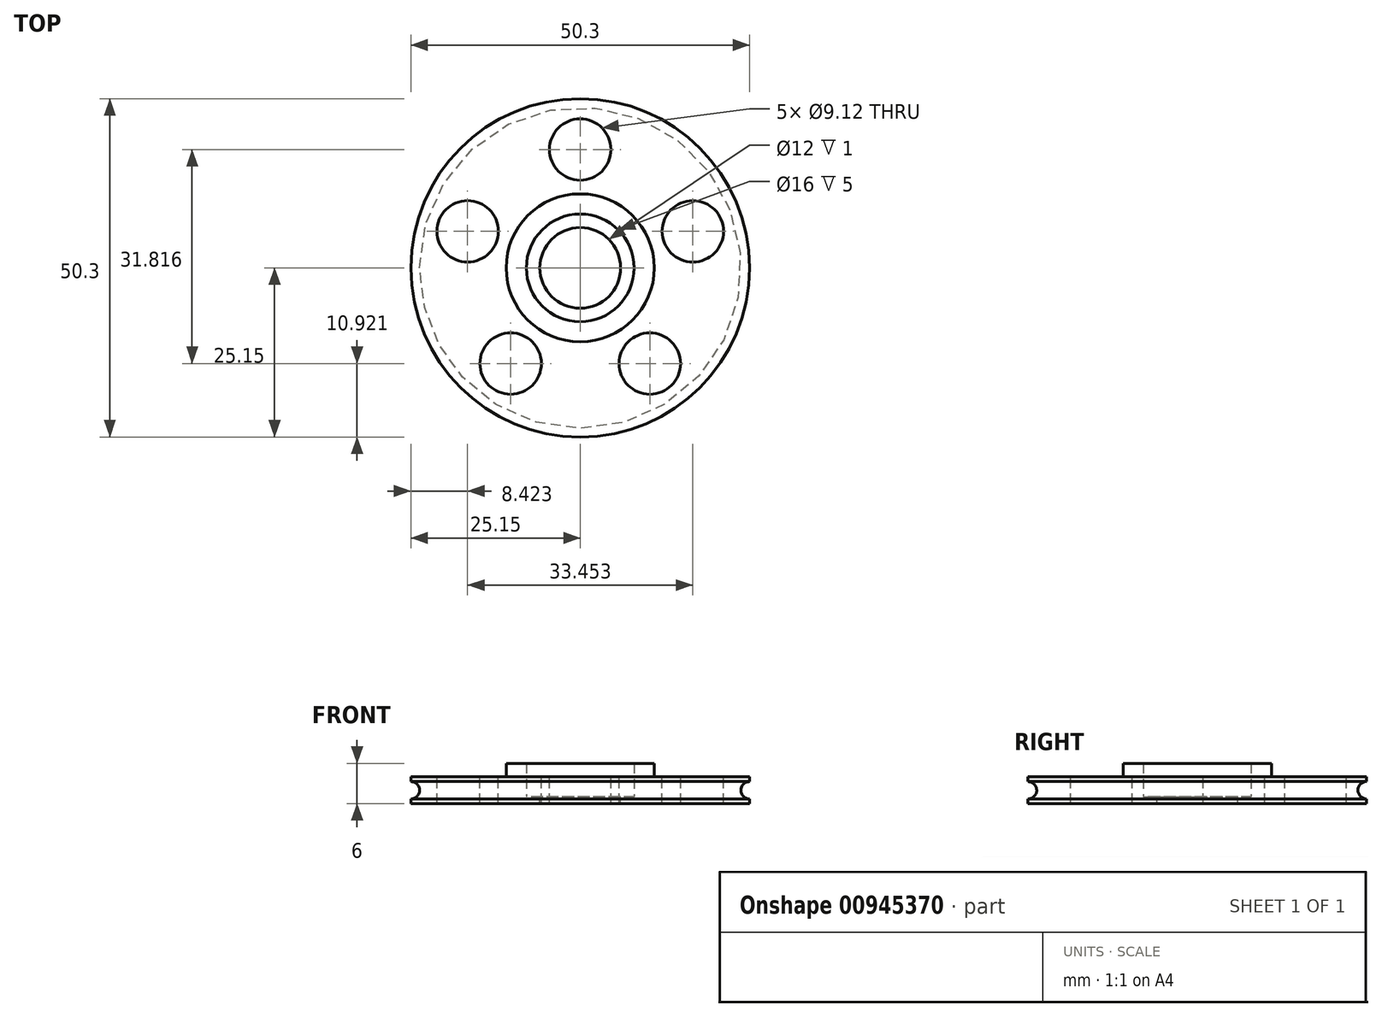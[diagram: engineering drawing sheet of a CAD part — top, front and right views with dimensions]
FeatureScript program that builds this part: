
annotation { "Feature Type Name" : "Feature", "Feature Type Description" : "" }
export const myFeature = defineFeature(function(context is Context, id is Id, definition is map)
    precondition{}
    {
        {
            var Q0;
            Q0=qCreatedBy(makeId("Top.planeOp"),FACE);
            var sketch = newSketch(context, id + "F0", { "sketchPlane" : qUnion([Q0])});
            skCircle(sketch, "E0", {"center": v(0, 0) * mm, "radius": 25.15 * mm});
            skSolve(sketch);
        }
        {
            var Q0;
            Q0=makeQuery(id+"F0.imprint","IMPRINT",FACE,{"disambiguationData":[TD([[makeQuery(id+"F0.imprint","IMPRINT",EDGE,{"derivedFrom":sQuery(id+"F0.wireOp",EDGE,"E0")}),1.0]])]});
            extrude(context, id + "F1", {"entities" : qUnion([Q0]), "depth" : 4 * mm, "offsetDistance" : 25.4 * mm});
        }
        {
            var Q0;
            Q0=makeQuery(id+"F1.opExtrude","CAP_FACE",FACE,{"disambiguationData":[OSD([sQuery(id+"F0.wireOp",EDGE,"E0"),sQuery(id+"F0.wireOp",EDGE,"n39IqKt5-bk1q-LU1x-fgod-8OyBNiFTd7FZ")])],"isStart":false});
            var sketch = newSketch(context, id + "F2", { "sketchPlane" : qUnion([Q0])});
            skCircle(sketch, "E1", {"center": v(0, 0) * mm, "radius": 8 * mm});
            skCircle(sketch, "E2.0", {"center": v(0, 0) * mm, "radius": 11 * mm});
            skSolve(sketch);
        }
        {
            var Q0;
            Q0=qSketchRegion(id+"F2",true);
            extrude(context, id + "F3", {"entities" : qUnion([Q0]), "operationType" : NewBodyOperationType.ADD, "flatOperationType" : FlatOperationType.REMOVE, "depth" : 2 * mm, "offsetDistance" : 25.4 * mm, "domain" : OperationDomain.MODEL});
        }
        {
            var Q0;
            Q0=makeQuery(id+"F3.boolean.opBoolean","SPLIT",FACE,{"disambiguationData":[TD([makeQuery(id+"F3.opExtrude","SWEPT_FACE",FACE,{"disambiguationData":[OSD([sQuery(id+"F2.wireOp",EDGE,"E1")])]})])],"derivedFrom":makeQuery(id+"F1.opExtrude","CAP_FACE",FACE,{"disambiguationData":[OSD([sQuery(id+"F0.wireOp",EDGE,"E0")])],"isStart":false})});
            var sketch = newSketch(context, id + "F4", { "sketchPlane" : qUnion([Q0])});
            skCircle(sketch, "E3", {"center": v(0, 0) * mm, "radius": 6 * mm});
            skSolve(sketch);
        }
        {
            var Q0;
            Q0=makeQuery(id+"F4.imprint","IMPRINT",FACE,{"disambiguationData":[TD([[makeQuery(id+"F4.imprint","IMPRINT",EDGE,{"derivedFrom":sQuery(id+"F4.wireOp",EDGE,"E3")}),1.0]])]});
            var Q1;
            Q1=makeQuery(id+"F4.imprint","IMPRINT",FACE,{"disambiguationData":[TD([[makeQuery(id+"F4.imprint","IMPRINT",EDGE,{"derivedFrom":makeQuery(id+"FgYK8jIepfClWtA_1.opExtrude","CAP_EDGE",EDGE,{"disambiguationData":[OSD([sQuery(id+"F8DXjnVyigKkjng_1.wireOp",EDGE,"EUjAMsCd-Zx2B-3j4q-cP5o-T3GrjTijNDqK")])],"isStart":false})}),1.0]])]});
            extrude(context, id + "F5", {"entities" : qUnion([Q0, Q1]), "operationType" : NewBodyOperationType.REMOVE, "oppositeDirection" : true, "depth" : 9 * mm, "offsetDistance" : 25.4 * mm});
        }
        {
            var Q0;
            Q0=qCreatedBy(makeId("Front.planeOp"),FACE);
            var sketch = newSketch(context, id + "F6", { "sketchPlane" : qUnion([Q0])});
            skCircle(sketch, "E4", {"center": v(-27.3, 2) * mm, "radius": 1.5 * mm});
            skLineSegment(sketch, "E5.bottom", {"start": v(-25.8, 0.65) * mm, "end": v(-27.95, 0.65) * mm});
            skLineSegment(sketch, "E5.top", {"start": v(-25.8, 3.35) * mm, "end": v(-27.95, 3.35) * mm});
            skLineSegment(sketch, "E5.left", {"start": v(-25.8, 0.65) * mm, "end": v(-25.8, 3.35) * mm});
            skLineSegment(sketch, "E5.right", {"start": v(-28.8, 1.91) * mm, "end": v(-28.8, 2.09) * mm});
            skLineSegment(sketch, "E6", {"start": v(0, 19.1) * mm, "end": v(0, -12.61) * mm, "construction": true});
            skLineSegment(sketch, "E7", {"start": v(-25.8, 1.83) * mm, "end": v(-25.81, 1.83) * mm});
            skPoint(sketch, "E8.orphan", {"position": v(-38.97, 3.35) * mm});
            skPoint(sketch, "E9.end.orphan", {"position": v(-15.64, 0.65) * mm});
            skPoint(sketch, "E9.start.orphan", {"position": v(-25.8, 2) * mm});
            skSolve(sketch);
        }
        {
            var Q0;
            {var subQ0=sQuery(id+"F6.wireOp",EDGE,"E5.top");var subQ1=sQuery(id+"F6.wireOp",EDGE,"E4");var subQ2=makeQuery(id+"F6.imprint","INTERSECT",VERTEX,{"disambiguationData":[OD(0.0)],"derivedFrom":[subQ1,subQ0]});Q0=makeQuery(id+"F6.imprint","IMPRINT",FACE,{"disambiguationData":[TD([[makeQuery(id+"F6.imprint","IMPRINT",EDGE,{"disambiguationData":[TD([[subQ2,1.0]])],"derivedFrom":subQ1}),1.0]])]});}
            var Q1;
            {var subQ0=sQuery(id+"F6.wireOp",EDGE,"E5.bottom");var subQ1=sQuery(id+"F6.wireOp",EDGE,"E4");var subQ2=makeQuery(id+"F6.imprint","INTERSECT",VERTEX,{"disambiguationData":[OD(0.0)],"derivedFrom":[subQ1,subQ0]});Q1=makeQuery(id+"F6.imprint","IMPRINT",FACE,{"disambiguationData":[TD([[makeQuery(id+"F6.imprint","IMPRINT",EDGE,{"disambiguationData":[TD([[subQ2,-1.0]])],"derivedFrom":subQ1}),1.0]])]});}
            var Q2;
            {var subQ4=sQuery(id+"F6.wireOp",EDGE,"E5.right");Q2=makeQuery(id+"F6.imprint","IMPRINT",FACE,{"disambiguationData":[TD([[makeQuery(id+"F6.imprint","IMPRINT",EDGE,{"derivedFrom":subQ4}),-1.0]])]});}
            var Q3;
            {var subQ0=sQuery(id+"F6.wireOp",EDGE,"p3G3spWP-JurA-dj01-Cwvm-HHlCDoPDIoxd");Q3=makeQuery(id+"F6.imprint","IMPRINT",FACE,{"disambiguationData":[TD([[makeQuery(id+"F6.imprint","IMPRINT",EDGE,{"derivedFrom":subQ0}),1.0]])]});}
            var Q4;
            Q4=makeQuery(id+"F6.imprint","IMPRINT",FACE,{"disambiguationData":[TD([[makeQuery(id+"F6.imprint","IMPRINT",EDGE,{"derivedFrom":sQuery(id+"F6.wireOp",EDGE,"p3G3spWP-JurA-dj01-Cwvm-HHlCDoPDIoxd")}),-1.0]])]});
            var Q5;
            {var subQ0=sQuery(id+"F6.wireOp",EDGE,"E9");Q5=makeQuery(id+"F6.imprint","IMPRINT",FACE,{"disambiguationData":[TD([[makeQuery(id+"F6.imprint","IMPRINT",EDGE,{"derivedFrom":subQ0}),1.0]])]});}
            var Q6;
            Q6=sQuery(id+"F6.wireOp",EDGE,"E6");
            revolve(context, id + "F7", {"operationType" : NewBodyOperationType.REMOVE, "surfaceOperationType" : NewSurfaceOperationType.NEW, "entities" : qUnion([Q0, Q1, Q2, Q3, Q4, Q5]), "axis" : qUnion([Q6]), "revolveType" : RevolveType.FULL, "oppositeDirection" : true});
        }
        {
            var Q0;
            Q0=makeQuery(id+"F3.boolean.opBoolean","SPLIT",FACE,{"disambiguationData":[TD([makeQuery(id+"F3.opExtrude","SWEPT_FACE",FACE,{"disambiguationData":[OSD([sQuery(id+"F2.wireOp",EDGE,"E1")])]})])],"derivedFrom":makeQuery(id+"F1.opExtrude","CAP_FACE",FACE,{"disambiguationData":[OSD([sQuery(id+"F0.wireOp",EDGE,"E0")])],"isStart":false})});
            extrude(context, id + "F8", {"entities" : qUnion([Q0]), "operationType" : NewBodyOperationType.REMOVE, "oppositeDirection" : true, "depth" : 3 * mm, "offsetDistance" : 25 * mm});
        }
        {
            var Q0;
            Q0=qCreatedBy(makeId("Front.planeOp"),FACE);
            var sketch = newSketch(context, id + "F9", { "sketchPlane" : qUnion([Q0])});
            skLineSegment(sketch, "E10", {"start": v(-25.14, 4) * mm, "end": v(-25.14, 0) * mm});
            skCircle(sketch, "E11", {"center": v(-25.14, 2) * mm, "radius": 1.28 * mm});
            skLineSegment(sketch, "E12", {"start": v(0, 9.34) * mm, "end": v(0, -3.6) * mm, "construction": true});
            skSolve(sketch);
        }
        {
            var Q0;
            {var subQ0=sQuery(id+"F9.wireOp",EDGE,"E11");var subQ1=sQuery(id+"F9.wireOp",EDGE,"E10");var subQ2=makeQuery(id+"F9.imprint","INTERSECT",VERTEX,{"disambiguationData":[OD(0.0)],"derivedFrom":[subQ1,subQ0]});Q0=makeQuery(id+"F9.imprint","IMPRINT",FACE,{"disambiguationData":[TD([[makeQuery(id+"F9.imprint","IMPRINT",EDGE,{"disambiguationData":[TD([[subQ2,1.0]])],"derivedFrom":subQ1}),1.0]])]});}
            var Q1;
            {var subQ0=sQuery(id+"F9.wireOp",EDGE,"E11");var subQ1=sQuery(id+"F9.wireOp",EDGE,"E10");var subQ2=makeQuery(id+"F9.imprint","INTERSECT",VERTEX,{"disambiguationData":[OD(0.0)],"derivedFrom":[subQ1,subQ0]});Q1=makeQuery(id+"F9.imprint","IMPRINT",FACE,{"disambiguationData":[TD([[makeQuery(id+"F9.imprint","IMPRINT",EDGE,{"disambiguationData":[TD([[subQ2,1.0]])],"derivedFrom":subQ1}),-1.0]])]});}
            var Q2;
            Q2=sQuery(id+"F9.wireOp",EDGE,"E12");
            revolve(context, id + "F10", {"operationType" : NewBodyOperationType.REMOVE, "surfaceOperationType" : NewSurfaceOperationType.NEW, "entities" : qUnion([Q0, Q1]), "axis" : qUnion([Q2]), "revolveType" : RevolveType.FULL, "oppositeDirection" : true});
        }
        {
            var Q0;
            {var subQ1=sQuery(id+"F0.wireOp",EDGE,"E0");var subQ2=makeQuery(id+"F1.opExtrude","SWEPT_FACE",FACE,{"disambiguationData":[OSD([subQ1])]});Q0=makeQuery(id+"FvaswZWDLJZ7FP9_1.boolean.opBoolean","SPLIT",FACE,{"disambiguationData":[TD([subQ2])],"derivedFrom":makeQuery(id+"F3.boolean.opBoolean","SPLIT",FACE,{"disambiguationData":[TD([subQ2])],"derivedFrom":makeQuery(id+"F1.opExtrude","CAP_FACE",FACE,{"disambiguationData":[OSD([subQ1])],"isStart":false})})});}
            var sketch = newSketch(context, id + "F11", { "sketchPlane" : qUnion([Q0])});
            skCircle(sketch, "E13", {"center": v(0, 17.59) * mm, "radius": 4.56 * mm});
            skCircle(sketch, "E14.1.0", {"center": v(-16.73, 5.43) * mm, "radius": 4.56 * mm});
            skCircle(sketch, "E14.2.0", {"center": v(-10.34, -14.23) * mm, "radius": 4.56 * mm});
            skCircle(sketch, "E14.3.0", {"center": v(10.34, -14.23) * mm, "radius": 4.56 * mm});
            skCircle(sketch, "E14.4.0", {"center": v(16.73, 5.43) * mm, "radius": 4.56 * mm});
            skPoint(sketch, "E14.center", {"position": v(0, 0) * mm});
            skSolve(sketch);
        }
        {
            var Q0;
            Q0=makeQuery(id+"F11.imprint","IMPRINT",FACE,{"disambiguationData":[TD([[makeQuery(id+"F11.imprint","IMPRINT",EDGE,{"derivedFrom":sQuery(id+"F11.wireOp",EDGE,"E13")}),1.0]])]});
            var Q1;
            Q1=makeQuery(id+"F11.imprint","IMPRINT",FACE,{"disambiguationData":[TD([[makeQuery(id+"F11.imprint","IMPRINT",EDGE,{"derivedFrom":sQuery(id+"F11.wireOp",EDGE,"E14.1.0")}),1.0]])]});
            var Q2;
            Q2=makeQuery(id+"F11.imprint","IMPRINT",FACE,{"disambiguationData":[TD([[makeQuery(id+"F11.imprint","IMPRINT",EDGE,{"derivedFrom":sQuery(id+"F11.wireOp",EDGE,"E14.2.0")}),1.0]])]});
            var Q3;
            Q3=makeQuery(id+"F11.imprint","IMPRINT",FACE,{"disambiguationData":[TD([[makeQuery(id+"F11.imprint","IMPRINT",EDGE,{"derivedFrom":sQuery(id+"F11.wireOp",EDGE,"E14.3.0")}),1.0]])]});
            var Q4;
            Q4=makeQuery(id+"F11.imprint","IMPRINT",FACE,{"disambiguationData":[TD([[makeQuery(id+"F11.imprint","IMPRINT",EDGE,{"derivedFrom":sQuery(id+"F11.wireOp",EDGE,"E14.4.0")}),1.0]])]});
            var Q5;
            Q5=makeQuery(id+"F11.imprint","IMPRINT",FACE,{"disambiguationData":[TD([[makeQuery(id+"F11.imprint","IMPRINT",EDGE,{"derivedFrom":sQuery(id+"F11.wireOp",EDGE,"7b7994cc-6478-41fd-ba13-783c76293075.1.5.0")}),1.0]])]});
            var Q6;
            Q6=makeQuery(id+"F11.imprint","IMPRINT",FACE,{"disambiguationData":[TD([[makeQuery(id+"F11.imprint","IMPRINT",EDGE,{"derivedFrom":sQuery(id+"F11.wireOp",EDGE,"853a8d3e-3d5b-4479-8794-f5eb44e94fe8.1.6.0")}),1.0]])]});
            extrude(context, id + "F12", {"entities" : qUnion([Q0, Q1, Q2, Q3, Q4, Q5, Q6]), "operationType" : NewBodyOperationType.REMOVE, "oppositeDirection" : true, "depth" : 25 * mm, "offsetDistance" : 25 * mm});
        }
    });
